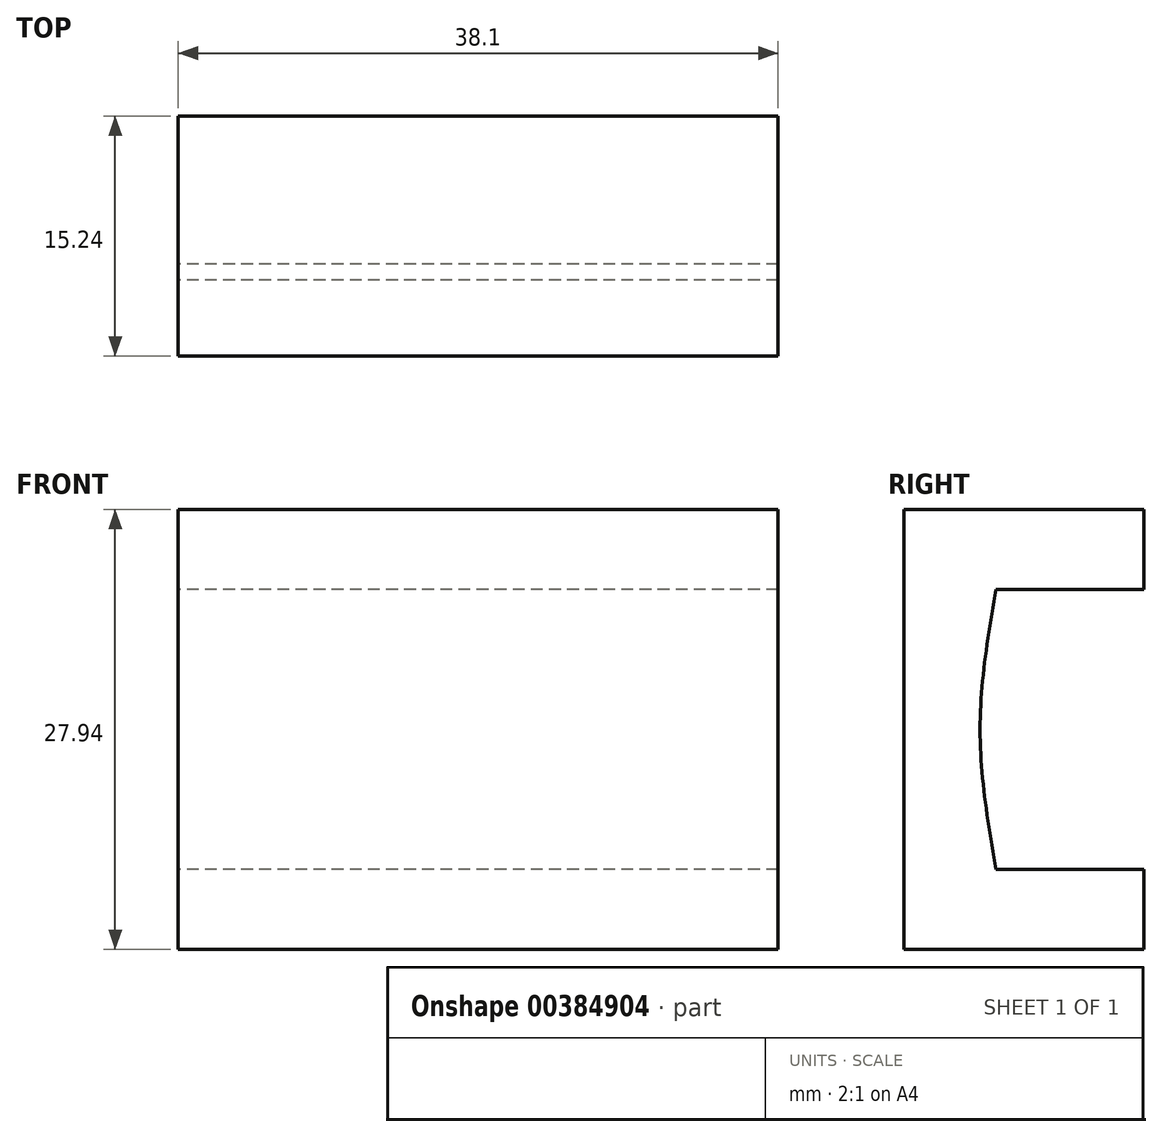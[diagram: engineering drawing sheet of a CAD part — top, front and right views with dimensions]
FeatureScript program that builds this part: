
annotation { "Feature Type Name" : "Feature", "Feature Type Description" : "" }
export const myFeature = defineFeature(function(context is Context, id is Id, definition is map)
    precondition{}
    {
        {
            var Q0;
            Q0=qCreatedBy(makeId("Top.planeOp"),FACE);
            var sketch = newSketch(context, id + "F0", { "sketchPlane" : qUnion([Q0])});
            skLineSegment(sketch, "E0.bottom", {"start": v(0, 0) * mm, "end": v(38.1, 0) * mm});
            skLineSegment(sketch, "E0.top", {"start": v(0, -15.24) * mm, "end": v(38.1, -15.24) * mm});
            skLineSegment(sketch, "E0.left", {"start": v(0, 0) * mm, "end": v(0, -15.24) * mm});
            skLineSegment(sketch, "E0.right", {"start": v(38.1, 0) * mm, "end": v(38.1, -15.24) * mm});
            skSolve(sketch);
        }
        {
            var Q0;
            Q0 = qSketchRegion(id + "F0", true);
            extrude(context, id + "F1", {"entities" : qUnion([Q0]), "depth" : 27.94 * mm});
        }
        {
            var Q0;
            Q0=makeQuery(id+"F1.opExtrude","SWEPT_FACE",FACE,{"disambiguationData":[OSD([sQuery(id+"F0.wireOp",EDGE,"E0.left")])]});
            var sketch = newSketch(context, id + "F2", { "sketchPlane" : qUnion([Q0])});
            skLineSegment(sketch, "E1", {"start": v(0, 0) * mm, "end": v(0, 5.08) * mm});
            skLineSegment(sketch, "E2", {"start": v(0, 5.08) * mm, "end": v(9.4, 5.08) * mm});
            skLineSegment(sketch, "E3", {"start": v(9.4, 22.86) * mm, "end": v(0, 22.86) * mm});
            skLineSegment(sketch, "E4", {"start": v(0, 22.86) * mm, "end": v(0, 5.08) * mm});
            skLineSegment(sketch, "E5", {"start": v(9.4, 22.86) * mm, "end": v(10.41, 22.86) * mm});
            skLineSegment(sketch, "E6", {"start": v(10.41, 22.86) * mm, "end": v(10.41, 13.97) * mm});
            skFitSpline(sketch, "E7", {"points": [v(9.4, 5.08) * mm, v(10.41, 13.97) * mm, v(9.4, 22.86) * mm], "startDerivative": vector(3.05, 17.78) * mm, "endDerivative": vector(-3.05, 17.78) * mm});
            skSolve(sketch);
        }
        {
            var Q0;
            {var subQ2=sQuery(id+"F2.wireOp",EDGE,"E2");Q0=makeQuery(id+"F2.imprint","IMPRINT",FACE,{"disambiguationData":[TD([[makeQuery(id+"F2.imprint","IMPRINT",EDGE,{"derivedFrom":subQ2}),1.0]])]});}
            extrude(context, id + "F3", {"entities" : qUnion([Q0]), "operationType" : NewBodyOperationType.REMOVE, "oppositeDirection" : true, "depth" : 38.1 * mm});
        }
    });
